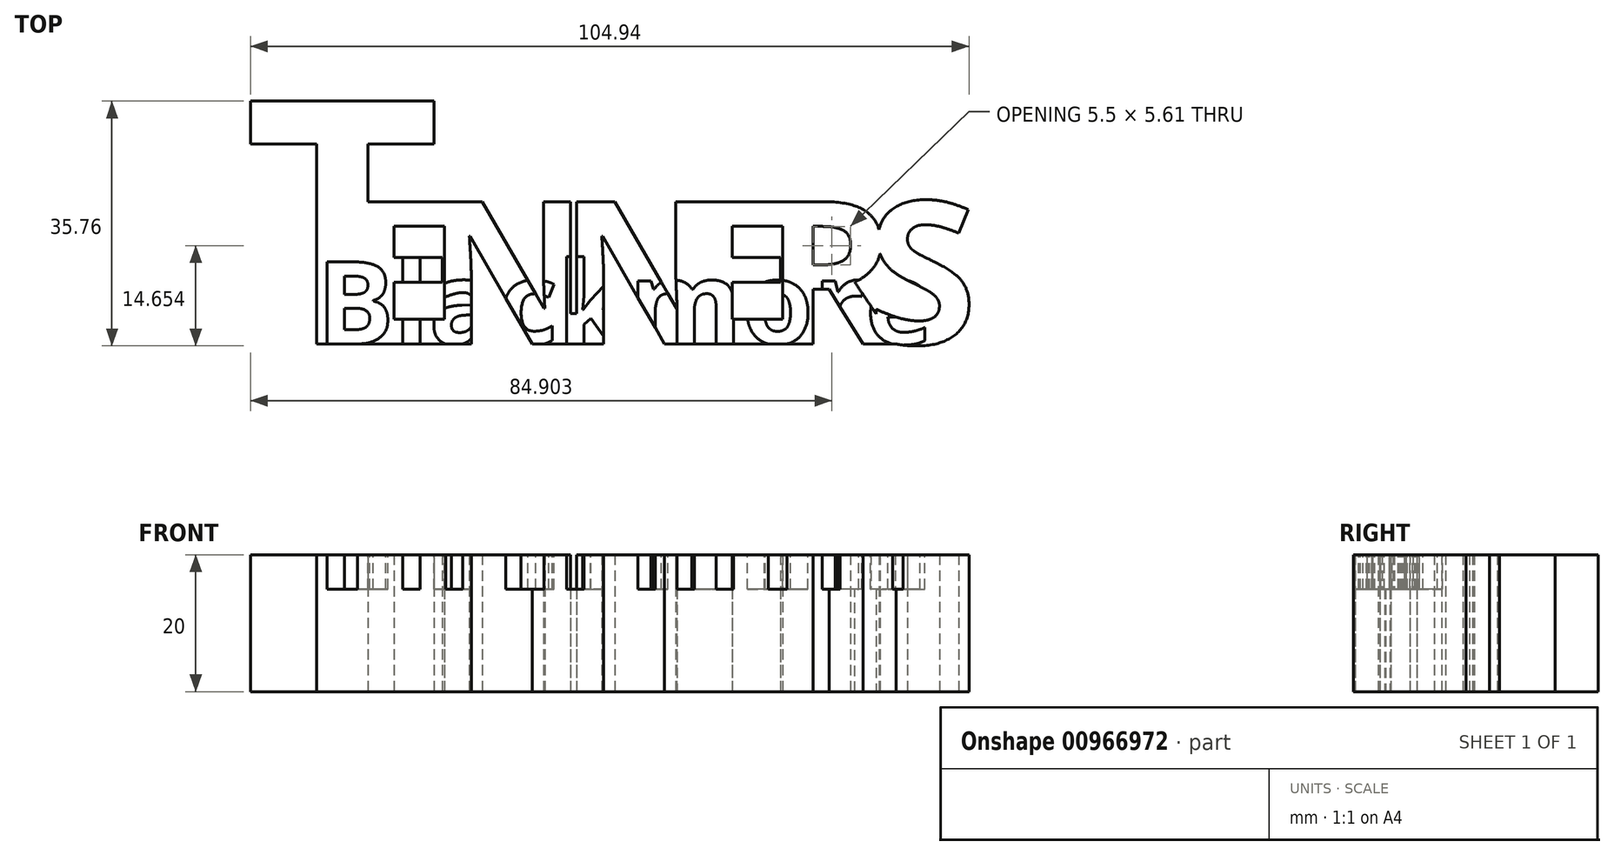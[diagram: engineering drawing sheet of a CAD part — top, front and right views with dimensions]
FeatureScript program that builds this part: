
annotation { "Feature Type Name" : "Feature", "Feature Type Description" : "" }
export const myFeature = defineFeature(function(context is Context, id is Id, definition is map)
    precondition{}
    {
        {
            var Q0;
            Q0=qCreatedBy(makeId("Top.planeOp"),FACE);
            var sketch = newSketch(context, id + "F0", { "sketchPlane" : qUnion([Q0])});
            skText(sketch, "E0", { "text": "T", "fontName": "OpenSans-Bold.ttf"});
            skText(sketch, "E1", { "text": "E", "fontName": "OpenSans-Bold.ttf"});
            skText(sketch, "E2", { "text": "N", "fontName": "OpenSans-Bold.ttf"});
            skText(sketch, "E3", { "text": "N", "fontName": "OpenSans-Bold.ttf"});
            skText(sketch, "E4", { "text": "E", "fontName": "OpenSans-Bold.ttf"});
            skText(sketch, "E5", { "text": "R", "fontName": "OpenSans-Bold.ttf"});
            skText(sketch, "E6", { "text": "S", "fontName": "OpenSans-Bold.ttf"});
            skLineSegment(sketch, "E7.bottom", {"start": v(-45, 0) * mm, "end": v(-43.88, 0) * mm});
            skLineSegment(sketch, "E7.top", {"start": v(-45, 4.42) * mm, "end": v(-43.88, 4.42) * mm});
            skLineSegment(sketch, "E7.left", {"start": v(-45, 0) * mm, "end": v(-45, 4.42) * mm});
            skLineSegment(sketch, "E7.right", {"start": v(-43.88, 0) * mm, "end": v(-43.88, 4.42) * mm});
            const initialGuessF0  = {"E0": [-0.09265, 0, 1, 0, 0.03577], "E1": [-0.07775, 0, 1, 0, 0.02096], "E2": [-0.06598, 0, 1, 0, 0.02096], "E3": [-0.04664, 0, 1, 0, 0.02096], "E4": [-0.0283, 0, 1, 0, 0.02096], "E5": [-0.01653, 0, 1, 0, 0.02096], "E6": [-0.0016, 0, 1, 0, 0.02096]};
            skSetInitialGuess(sketch, initialGuessF0);
            skSolve(sketch);
        }
        {
            var Q0;
            Q0 = qSketchRegion(id + "F0", true);
            extrude(context, id + "F1", {"entities" : qUnion([Q0]), "depth" : 20 * mm, "offsetDistance" : 25 * mm});
        }
        {
            var Q0;
            Q0=makeQuery(id+"F1.opExtrude","CAP_FACE",FACE,{"disambiguationData":[OSD([sQuery(id+"F0.wireOp",EDGE,"E0.sketch_text.stroke-0"),sQuery(id+"F0.wireOp",EDGE,"E0.sketch_text.stroke-1"),sQuery(id+"F0.wireOp",EDGE,"E0.sketch_text.stroke-2"),sQuery(id+"F0.wireOp",EDGE,"E0.sketch_text.stroke-3"),sQuery(id+"F0.wireOp",EDGE,"E0.sketch_text.stroke-4"),sQuery(id+"F0.wireOp",EDGE,"E0.sketch_text.stroke-5"),sQuery(id+"F0.wireOp",EDGE,"E0.sketch_text.stroke-6"),sQuery(id+"F0.wireOp",EDGE,"E0.sketch_text.stroke-7"),sQuery(id+"F0.wireOp",EDGE,"E1.sketch_text.stroke-0"),sQuery(id+"F0.wireOp",EDGE,"E1.sketch_text.stroke-2"),sQuery(id+"F0.wireOp",EDGE,"E1.sketch_text.stroke-4"),sQuery(id+"F0.wireOp",EDGE,"E1.sketch_text.stroke-5"),sQuery(id+"F0.wireOp",EDGE,"E1.sketch_text.stroke-6"),sQuery(id+"F0.wireOp",EDGE,"E1.sketch_text.stroke-7"),sQuery(id+"F0.wireOp",EDGE,"E1.sketch_text.stroke-8"),sQuery(id+"F0.wireOp",EDGE,"E1.sketch_text.stroke-9"),sQuery(id+"F0.wireOp",EDGE,"E1.sketch_text.stroke-10"),sQuery(id+"F0.wireOp",EDGE,"E2.sketch_text.stroke-0"),sQuery(id+"F0.wireOp",EDGE,"E2.sketch_text.stroke-1"),sQuery(id+"F0.wireOp",EDGE,"E2.sketch_text.stroke-2"),sQuery(id+"F0.wireOp",EDGE,"E2.sketch_text.stroke-3"),sQuery(id+"F0.wireOp",EDGE,"E2.sketch_text.stroke-4"),sQuery(id+"F0.wireOp",EDGE,"E2.sketch_text.stroke-5"),sQuery(id+"F0.wireOp",EDGE,"E2.sketch_text.stroke-6"),sQuery(id+"F0.wireOp",EDGE,"E2.sketch_text.stroke-7"),sQuery(id+"F0.wireOp",EDGE,"E2.sketch_text.stroke-8"),sQuery(id+"F0.wireOp",EDGE,"E2.sketch_text.stroke-9"),sQuery(id+"F0.wireOp",EDGE,"E2.sketch_text.stroke-10"),sQuery(id+"F0.wireOp",EDGE,"E2.sketch_text.stroke-11"),sQuery(id+"F0.wireOp",EDGE,"E2.sketch_text.stroke-12"),sQuery(id+"F0.wireOp",EDGE,"E2.sketch_text.stroke-13"),sQuery(id+"F0.wireOp",EDGE,"E3.sketch_text.stroke-0"),sQuery(id+"F0.wireOp",EDGE,"E3.sketch_text.stroke-1"),sQuery(id+"F0.wireOp",EDGE,"E3.sketch_text.stroke-2"),sQuery(id+"F0.wireOp",EDGE,"E3.sketch_text.stroke-3"),sQuery(id+"F0.wireOp",EDGE,"E3.sketch_text.stroke-4"),sQuery(id+"F0.wireOp",EDGE,"E3.sketch_text.stroke-5"),sQuery(id+"F0.wireOp",EDGE,"E3.sketch_text.stroke-6"),sQuery(id+"F0.wireOp",EDGE,"E3.sketch_text.stroke-7"),sQuery(id+"F0.wireOp",EDGE,"E3.sketch_text.stroke-8"),sQuery(id+"F0.wireOp",EDGE,"E3.sketch_text.stroke-9"),sQuery(id+"F0.wireOp",EDGE,"E3.sketch_text.stroke-10"),sQuery(id+"F0.wireOp",EDGE,"E3.sketch_text.stroke-11"),sQuery(id+"F0.wireOp",EDGE,"E3.sketch_text.stroke-12"),sQuery(id+"F0.wireOp",EDGE,"E4.sketch_text.stroke-0"),sQuery(id+"F0.wireOp",EDGE,"E4.sketch_text.stroke-2"),sQuery(id+"F0.wireOp",EDGE,"E4.sketch_text.stroke-4"),sQuery(id+"F0.wireOp",EDGE,"E4.sketch_text.stroke-5"),sQuery(id+"F0.wireOp",EDGE,"E4.sketch_text.stroke-6"),sQuery(id+"F0.wireOp",EDGE,"E4.sketch_text.stroke-7"),sQuery(id+"F0.wireOp",EDGE,"E4.sketch_text.stroke-8"),sQuery(id+"F0.wireOp",EDGE,"E4.sketch_text.stroke-9"),sQuery(id+"F0.wireOp",EDGE,"E4.sketch_text.stroke-10"),sQuery(id+"F0.wireOp",EDGE,"E5.sketch_text.stroke-0"),sQuery(id+"F0.wireOp",EDGE,"E5.sketch_text.stroke-1"),sQuery(id+"F0.wireOp",EDGE,"E5.sketch_text.stroke-2"),sQuery(id+"F0.wireOp",EDGE,"E5.sketch_text.stroke-3"),sQuery(id+"F0.wireOp",EDGE,"E5.sketch_text.stroke-4"),sQuery(id+"F0.wireOp",EDGE,"E5.sketch_text.stroke-5"),sQuery(id+"F0.wireOp",EDGE,"E5.sketch_text.stroke-6"),sQuery(id+"F0.wireOp",EDGE,"E5.sketch_text.stroke-7"),sQuery(id+"F0.wireOp",EDGE,"E5.sketch_text.stroke-8"),sQuery(id+"F0.wireOp",EDGE,"E5.sketch_text.stroke-9"),sQuery(id+"F0.wireOp",EDGE,"E5.sketch_text.stroke-10"),sQuery(id+"F0.wireOp",EDGE,"E5.sketch_text.stroke-11"),sQuery(id+"F0.wireOp",EDGE,"E5.sketch_text.stroke-12"),sQuery(id+"F0.wireOp",EDGE,"E5.sketch_text.stroke-13"),sQuery(id+"F0.wireOp",EDGE,"E5.sketch_text.stroke-14"),sQuery(id+"F0.wireOp",EDGE,"E5.sketch_text.stroke-15"),sQuery(id+"F0.wireOp",EDGE,"E5.sketch_text.stroke-16"),sQuery(id+"F0.wireOp",EDGE,"E5.sketch_text.stroke-17"),sQuery(id+"F0.wireOp",EDGE,"E5.sketch_text.stroke-18"),sQuery(id+"F0.wireOp",EDGE,"E6.sketch_text.stroke-0"),sQuery(id+"F0.wireOp",EDGE,"E6.sketch_text.stroke-1"),sQuery(id+"F0.wireOp",EDGE,"E6.sketch_text.stroke-2"),sQuery(id+"F0.wireOp",EDGE,"E6.sketch_text.stroke-3"),sQuery(id+"F0.wireOp",EDGE,"E6.sketch_text.stroke-4"),sQuery(id+"F0.wireOp",EDGE,"E6.sketch_text.stroke-5"),sQuery(id+"F0.wireOp",EDGE,"E6.sketch_text.stroke-6"),sQuery(id+"F0.wireOp",EDGE,"E6.sketch_text.stroke-7"),sQuery(id+"F0.wireOp",EDGE,"E6.sketch_text.stroke-8"),sQuery(id+"F0.wireOp",EDGE,"E6.sketch_text.stroke-9"),sQuery(id+"F0.wireOp",EDGE,"E6.sketch_text.stroke-10"),sQuery(id+"F0.wireOp",EDGE,"E6.sketch_text.stroke-11"),sQuery(id+"F0.wireOp",EDGE,"E6.sketch_text.stroke-12"),sQuery(id+"F0.wireOp",EDGE,"E6.sketch_text.stroke-13"),sQuery(id+"F0.wireOp",EDGE,"E6.sketch_text.stroke-14"),sQuery(id+"F0.wireOp",EDGE,"E6.sketch_text.stroke-15"),sQuery(id+"F0.wireOp",EDGE,"E6.sketch_text.stroke-16"),sQuery(id+"F0.wireOp",EDGE,"E6.sketch_text.stroke-17"),sQuery(id+"F0.wireOp",EDGE,"E6.sketch_text.stroke-18"),sQuery(id+"F0.wireOp",EDGE,"E6.sketch_text.stroke-19"),sQuery(id+"F0.wireOp",EDGE,"E6.sketch_text.stroke-20"),sQuery(id+"F0.wireOp",EDGE,"E6.sketch_text.stroke-21"),sQuery(id+"F0.wireOp",EDGE,"E6.sketch_text.stroke-22"),sQuery(id+"F0.wireOp",EDGE,"E6.sketch_text.stroke-23"),sQuery(id+"F0.wireOp",EDGE,"E6.sketch_text.stroke-24"),sQuery(id+"F0.wireOp",EDGE,"E6.sketch_text.stroke-25"),sQuery(id+"F0.wireOp",EDGE,"E6.sketch_text.stroke-26"),sQuery(id+"F0.wireOp",EDGE,"E6.sketch_text.stroke-27"),sQuery(id+"F0.wireOp",EDGE,"E7.bottom"),sQuery(id+"F0.wireOp",EDGE,"E7.top")])],"isStart":false});
            var sketch = newSketch(context, id + "F2", { "sketchPlane" : qUnion([Q0])});
            skText(sketch, "E8", { "text": "Blackmore", "fontName": "OpenSans-Bold.ttf"});
            const initialGuessF2  = {"E8": [-0.08202, 0, 1, 0, 0.0121]};
            skSetInitialGuess(sketch, initialGuessF2);
            skSolve(sketch);
        }
        {
            var Q0;
            Q0 = qSketchRegion(id + "F2", true);
            extrude(context, id + "F3", {"entities" : qUnion([Q0]), "operationType" : NewBodyOperationType.REMOVE, "oppositeDirection" : true, "depth" : 5 * mm, "offsetDistance" : 25 * mm});
        }
    });
